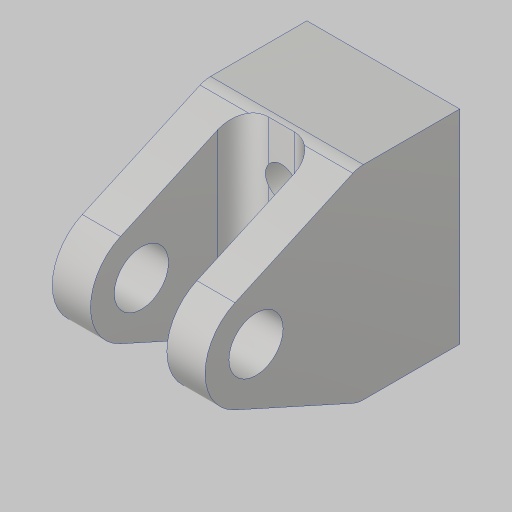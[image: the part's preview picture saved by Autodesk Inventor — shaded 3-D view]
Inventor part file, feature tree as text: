
AUTODESK INVENTOR PART (.ipt)
format: ipt  version: 2023.5 (Build 275446000, 446)  size: 178,688 bytes
history: native  units: in
note: dims shown in document units (in); Inventor stores cm internally (conversion verified against a paired STEP export)
features: sketch x3, projected_geometry x3, extrude x2, hole x2, fillet x1
ambient origin geometry x8: Origin, YZ Plane, XZ Plane, XY Plane, X Axis, Y Axis, Z Axis, Center Point
bodies: Solid1 (feature_tree)
feature tree (11):
  sketch  "Sketch1"  dims[d0=1.0in d1=0.5in]
  extrude  "Extrusion1"  Depth=0.5in
  hole  "Hole1"  [1 undecoded]
  hole  "Hole2"  [1 undecoded]
  extrude  "Extrusion2"  Depth=0.125in
  fillet  "Fillet1"  Radius=0.75in
  sketch  "Sketch2"  dims[d2=0.5in d3=0.5in]
  sketch  "Sketch3"  dims[d4=0.75in d5=0.0in d6=0.266in d7=0.38in d8=0.507in d9=0.25in d10=0.5635in d11=0.536in d12=0.8108in d13=0.5in d14=0.156in d15=0.38in d16=0.375in d17=0.25in d18=0.5635in d19=0.536in d20=0.8108in d21=0.375in d22=0.75in d23=0.0in d24=0.0in d25=0.125in]
  projected_geometry  "Projected Loop1"
  projected_geometry  "Projected Loop2"
  projected_geometry  "Projected Loop3"
note: 2 required parameter values undecoded (feature->parameter linkage not recoverable at this tier; creation-order binding heuristic only, values carry confidence <= 0.55)
